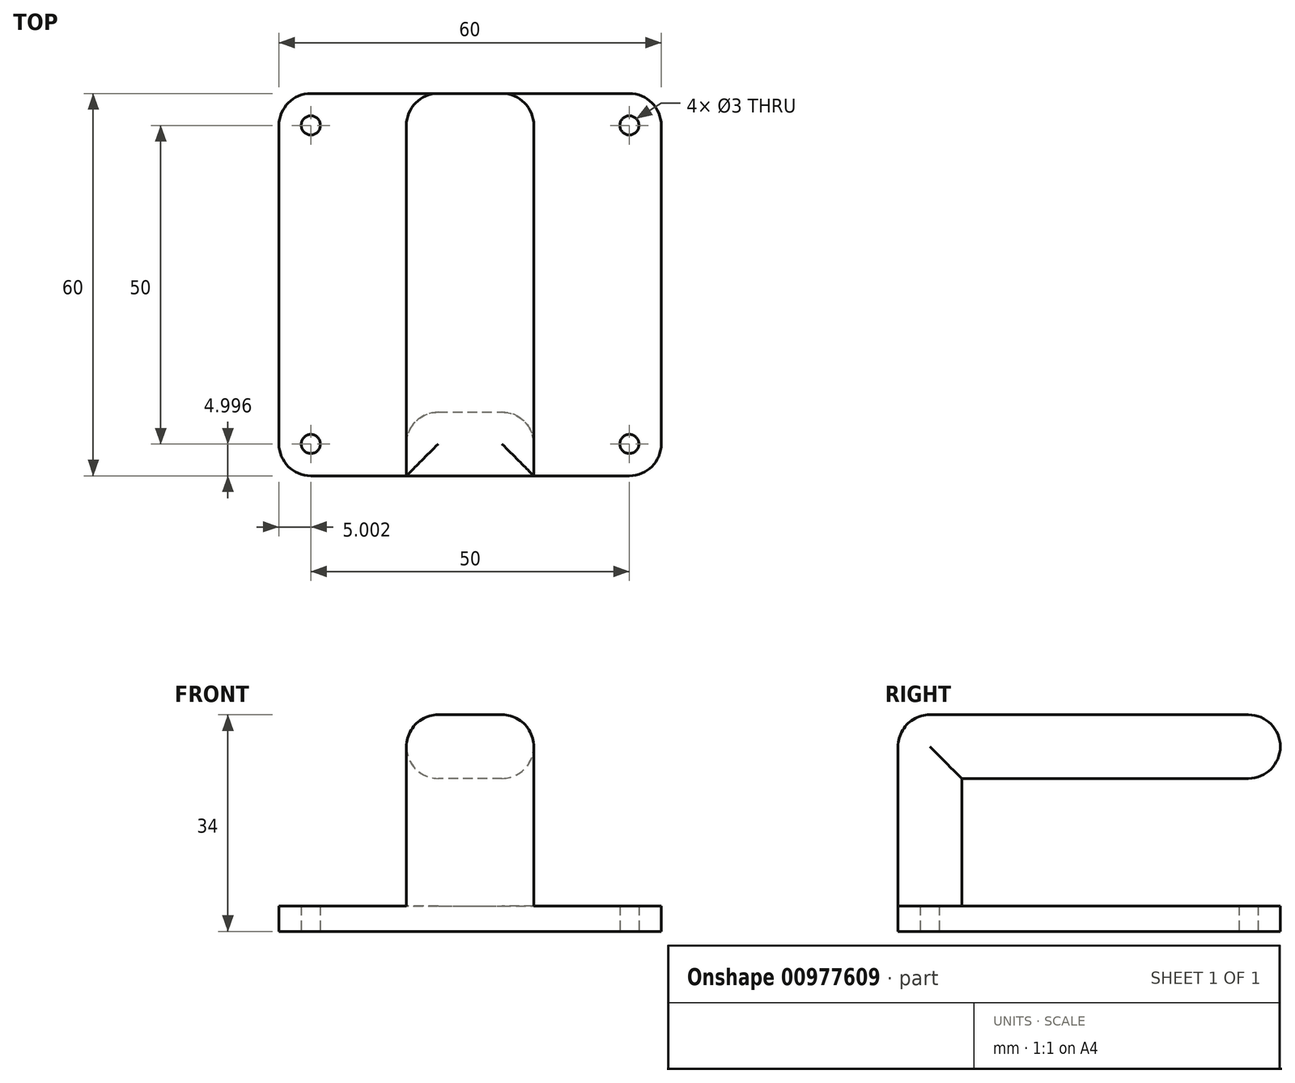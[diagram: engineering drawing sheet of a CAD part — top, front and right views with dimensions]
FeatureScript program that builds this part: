
annotation { "Feature Type Name" : "Feature", "Feature Type Description" : "" }
export const myFeature = defineFeature(function(context is Context, id is Id, definition is map)
    precondition{}
    {
        {
            var Q0;
            Q0=qCreatedBy(makeId("Top.planeOp"),FACE);
            var sketch = newSketch(context, id + "F0", { "sketchPlane" : qUnion([Q0])});
            skLineSegment(sketch, "E0.bottom", {"start": v(-23.83, 27.22) * mm, "end": v(26.17, 27.22) * mm});
            skLineSegment(sketch, "E0.top", {"start": v(-23.83, -32.78) * mm, "end": v(26.17, -32.78) * mm});
            skLineSegment(sketch, "E0.left", {"start": v(-28.83, 22.22) * mm, "end": v(-28.83, -27.78) * mm});
            skLineSegment(sketch, "E0.right", {"start": v(31.17, 22.22) * mm, "end": v(31.17, -27.78) * mm});
            skPoint(sketch, "E1.visualSharp", {"position": v(-28.83, 27.22) * mm});
            skArc(sketch, "E1.filletArc", {"start": v(-23.83, 27.22) * mm, "mid": v(-27.36, 25.75) * mm, "end": v(-28.83, 22.22) * mm});
            skPoint(sketch, "E2.visualSharp", {"position": v(-28.83, -32.78) * mm});
            skArc(sketch, "E2.filletArc", {"start": v(-28.83, -27.78) * mm, "mid": v(-27.36, -31.32) * mm, "end": v(-23.83, -32.78) * mm});
            skPoint(sketch, "E3.visualSharp", {"position": v(31.17, 27.22) * mm});
            skArc(sketch, "E3.filletArc", {"start": v(31.17, 22.22) * mm, "mid": v(29.7, 25.75) * mm, "end": v(26.17, 27.22) * mm});
            skPoint(sketch, "E4.visualSharp", {"position": v(31.17, -32.78) * mm});
            skArc(sketch, "E4.filletArc", {"start": v(26.17, -32.78) * mm, "mid": v(29.7, -31.32) * mm, "end": v(31.17, -27.78) * mm});
            skCircle(sketch, "E5", {"center": v(-23.83, 22.22) * mm, "radius": 1.5 * mm});
            skLineSegment(sketch, "E6", {"start": v(1.17, 27.22) * mm, "end": v(1.17, -2.78) * mm, "construction": true});
            skLineSegment(sketch, "E7", {"start": v(-28.83, -2.78) * mm, "end": v(1.17, -2.78) * mm, "construction": true});
            skCircle(sketch, "E8.MirrorC", {"center": v(26.17, 22.22) * mm, "radius": 1.5 * mm});
            skCircle(sketch, "E9.MirrorC", {"center": v(-23.83, -27.78) * mm, "radius": 1.5 * mm});
            skCircle(sketch, "E10.MirrorC", {"center": v(26.17, -27.78) * mm, "radius": 1.5 * mm});
            skSolve(sketch);
        }
        {
            var Q0;
            Q0=makeQuery(id+"F0.imprint","IMPRINT",FACE,{"disambiguationData":[TD([[makeQuery(id+"F0.imprint","IMPRINT",EDGE,{"derivedFrom":sQuery(id+"F0.wireOp",EDGE,"E0.bottom")}),-1.0]])]});
            extrude(context, id + "F1", {"entities" : qUnion([Q0]), "depth" : 4 * mm, "offsetDistance" : 25 * mm});
        }
        {
            var Q0;
            Q0=makeQuery(id+"F1.opExtrude","CAP_FACE",FACE,{"disambiguationData":[OSD([sQuery(id+"F0.wireOp",EDGE,"E0.bottom"),sQuery(id+"F0.wireOp",EDGE,"E0.top"),sQuery(id+"F0.wireOp",EDGE,"E0.left"),sQuery(id+"F0.wireOp",EDGE,"E0.right"),sQuery(id+"F0.wireOp",EDGE,"E1.filletArc"),sQuery(id+"F0.wireOp",EDGE,"E2.filletArc"),sQuery(id+"F0.wireOp",EDGE,"E3.filletArc"),sQuery(id+"F0.wireOp",EDGE,"E4.filletArc"),sQuery(id+"F0.wireOp",EDGE,"E5"),sQuery(id+"F0.wireOp",EDGE,"E8.MirrorC"),sQuery(id+"F0.wireOp",EDGE,"E9.MirrorC"),sQuery(id+"F0.wireOp",EDGE,"E10.MirrorC")])],"isStart":false});
            var sketch = newSketch(context, id + "F2", { "sketchPlane" : qUnion([Q0])});
            skLineSegment(sketch, "E11", {"start": v(1.17, 27.22) * mm, "end": v(1.17, -22.78) * mm});
            skLineSegment(sketch, "E12", {"start": v(1.17, -32.78) * mm, "end": v(-8.83, -32.78) * mm});
            skLineSegment(sketch, "E13", {"start": v(-8.83, -32.78) * mm, "end": v(11.17, -32.78) * mm});
            skLineSegment(sketch, "E14", {"start": v(11.17, -32.78) * mm, "end": v(11.17, -22.78) * mm});
            skLineSegment(sketch, "E15", {"start": v(11.17, 27.22) * mm, "end": v(-8.83, 27.22) * mm});
            skLineSegment(sketch, "E16", {"start": v(-8.83, -22.78) * mm, "end": v(-8.83, -32.78) * mm});
            skLineSegment(sketch, "E17", {"start": v(-8.83, -32.78) * mm, "end": v(-8.83, -22.78) * mm});
            skLineSegment(sketch, "E18", {"start": v(-8.83, -22.78) * mm, "end": v(11.17, -22.78) * mm});
            skSolve(sketch);
        }
        {
            var Q0;
            {var subQ1=sQuery(id+"F2.wireOp",EDGE,"E14");Q0=makeQuery(id+"F2.imprint","IMPRINT",FACE,{"disambiguationData":[TD([[makeQuery(id+"F2.imprint","IMPRINT",EDGE,{"derivedFrom":subQ1}),1.0]])]});}
            extrude(context, id + "F3", {"entities" : qUnion([Q0]), "operationType" : NewBodyOperationType.ADD, "depth" : 30 * mm, "offsetDistance" : 25 * mm});
        }
        {
            var Q0;
            Q0=makeQuery(id+"F3.opExtrude","SWEPT_FACE",FACE,{"disambiguationData":[OSD([sQuery(id+"F2.wireOp",EDGE,"E18")])]});
            var sketch = newSketch(context, id + "F4", { "sketchPlane" : qUnion([Q0])});
            skLineSegment(sketch, "E19.bottom", {"start": v(-11.17, 34) * mm, "end": v(8.83, 34) * mm});
            skLineSegment(sketch, "E19.top", {"start": v(-11.17, 24) * mm, "end": v(8.83, 24) * mm});
            skLineSegment(sketch, "E19.left", {"start": v(-11.17, 34) * mm, "end": v(-11.17, 24) * mm});
            skLineSegment(sketch, "E19.right", {"start": v(8.83, 34) * mm, "end": v(8.83, 24) * mm});
            skSolve(sketch);
        }
        {
            var Q0;
            Q0 = qSketchRegion(id + "F4", true);
            extrude(context, id + "F5", {"entities" : qUnion([Q0]), "operationType" : NewBodyOperationType.ADD, "depth" : 50 * mm, "offsetDistance" : 25 * mm});
        }
        {
            var Q0;
            Q0=makeQuery(id+"F3.opExtrude","CAP_EDGE",EDGE,{"disambiguationData":[OSD([sQuery(id+"F2.wireOp",EDGE,"E18")])],"isStart":true});
            var Q1;
            Q1=makeQuery(id+"F3.opExtrude","SWEPT_EDGE",EDGE,{"disambiguationData":[OSD([sQuery(id+"F2.wireOp",EDGE,"E17"),sQuery(id+"F2.wireOp",EDGE,"E18")])]});
            var Q2;
            Q2=makeQuery(id+"F5.opExtrude","SWEPT_EDGE",EDGE,{"disambiguationData":[OSD([sQuery(id+"F2.wireOp",EDGE,"E17"),sQuery(id+"F2.wireOp",EDGE,"E18"),sQuery(id+"F4.wireOp",EDGE,"E19.top"),sQuery(id+"F4.wireOp",EDGE,"E19.right")])]});
            var Q3;
            Q3=makeQuery(id+"F5.opExtrude","SWEPT_EDGE",EDGE,{"disambiguationData":[OSD([sQuery(id+"F2.wireOp",EDGE,"E14"),sQuery(id+"F2.wireOp",EDGE,"E18"),sQuery(id+"F4.wireOp",EDGE,"E19.top"),sQuery(id+"F4.wireOp",EDGE,"E19.left")])]});
            var Q4;
            Q4=makeQuery(id+"F5.opExtrude","CAP_FACE",FACE,{"disambiguationData":[OSD([sQuery(id+"F4.wireOp",EDGE,"E19.bottom"),sQuery(id+"F4.wireOp",EDGE,"E19.top"),sQuery(id+"F4.wireOp",EDGE,"E19.left"),sQuery(id+"F4.wireOp",EDGE,"E19.right")])],"isStart":false});
            var Q5;
            Q5=makeQuery(id+"F3.opExtrude","CAP_EDGE",EDGE,{"disambiguationData":[OSD([sQuery(id+"F2.wireOp",EDGE,"E13")])],"isStart":false});
            var Q6;
            Q6=makeQuery(id+"F5.boolean.opBoolean","MERGE",EDGE,{"derivedFrom":[makeQuery(id+"F3.opExtrude","CAP_EDGE",EDGE,{"disambiguationData":[OSD([sQuery(id+"F2.wireOp",EDGE,"E17")])],"isStart":false}),makeQuery(id+"F5.opExtrude","SWEPT_EDGE",EDGE,{"disambiguationData":[OSD([sQuery(id+"F4.wireOp",EDGE,"E19.bottom"),sQuery(id+"F4.wireOp",EDGE,"E19.right")])]})]});
            var Q7;
            Q7=makeQuery(id+"F5.boolean.opBoolean","MERGE",EDGE,{"derivedFrom":[makeQuery(id+"F3.opExtrude","CAP_EDGE",EDGE,{"disambiguationData":[OSD([sQuery(id+"F2.wireOp",EDGE,"E14")])],"isStart":false}),makeQuery(id+"F5.opExtrude","SWEPT_EDGE",EDGE,{"disambiguationData":[OSD([sQuery(id+"F4.wireOp",EDGE,"E19.bottom"),sQuery(id+"F4.wireOp",EDGE,"E19.left")])]})]});
            var Q8;
            Q8=makeQuery(id+"F5.opExtrude","CAP_EDGE",EDGE,{"disambiguationData":[OSD([sQuery(id+"F4.wireOp",EDGE,"E19.top")])],"isStart":true});
            fillet(context, id + "F6", {"entities" : qUnion([Q0, Q1, Q2, Q3, Q4, Q5, Q6, Q7, Q8]), "radius" : 5 * mm, "tangentPropagation" : true, "allowEdgeOverflow" : false});
        }
    });
